# Revit family: Namika robe hook - cabinetry knob_RFA
name_source: partatom
category: Generic Models
units: mm (PartAtom-declared; Revit-internal decimal feet)

## family parameters
Always vertical = Yes
Can host rebar = No
Cut with Voids When Loaded = No
Maintain Annotation Orientation = No
OmniClass Number = 23.21.15.19.13
Part Type = Normal
Room Calculation Point = No
Round Connector Dimension = Use Diameter
Shared = No
Work Plane-Based = No

## types (1)
- Standard
    Category = Accessory
    Default Elevation = 0 mm  [stored 0 ft]
    Description = Namika Robe Hook/Cabinetry Knob
    Keywords = Robe Hook, Cabinetry Knob, Reeded
    Manufacturer = Abi Interiors Pty Ltd
    Part Number = Brushed Brass (15671), Brushed Copper (15672), Brushed Gunmetal (15673), Brushed Nickel (15674)
    Project = Namika Collection
    QR Link = abi.guide/Nami_Robe_Hook_Cab_Pull
    Spec Image = https://cdn.bfldr.com
    Title = Namika Robe Hook/ Cabinetry Knob

note: [stored X ft] marks values corroborated as IEEE doubles in the binary element streams (Revit-internal decimal feet)

## geometry (parser evidence)
native form markers: Sweep x3
no freeform markers — native parametric forms only
